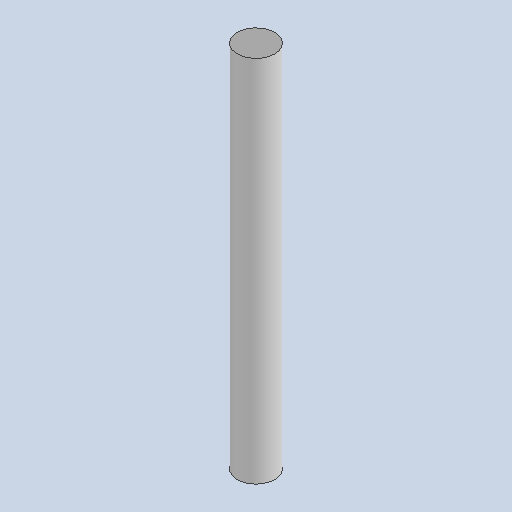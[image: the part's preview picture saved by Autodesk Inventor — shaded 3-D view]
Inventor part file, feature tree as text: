
AUTODESK INVENTOR PART (.ipt)
format: ipt  version: 2025 (Build 290162010, 162A)  size: 79,360 bytes
history: native  units: mm
features: extrude x1, sketch x1
ambient origin geometry x8: Origin, YZ Plane, XZ Plane, XY Plane, X Axis, Y Axis, Z Axis, Center Point
bodies: Solid1 (feature_tree)
feature tree (2):
  extrude  "Extrusion1"  Depth=118.0mm TaperAngle=0.0deg
  sketch  "Sketch1"  dims[d0=12.0mm d1=118.0mm d2=40.0mm d3=0.0mm d4=0.0mm]
